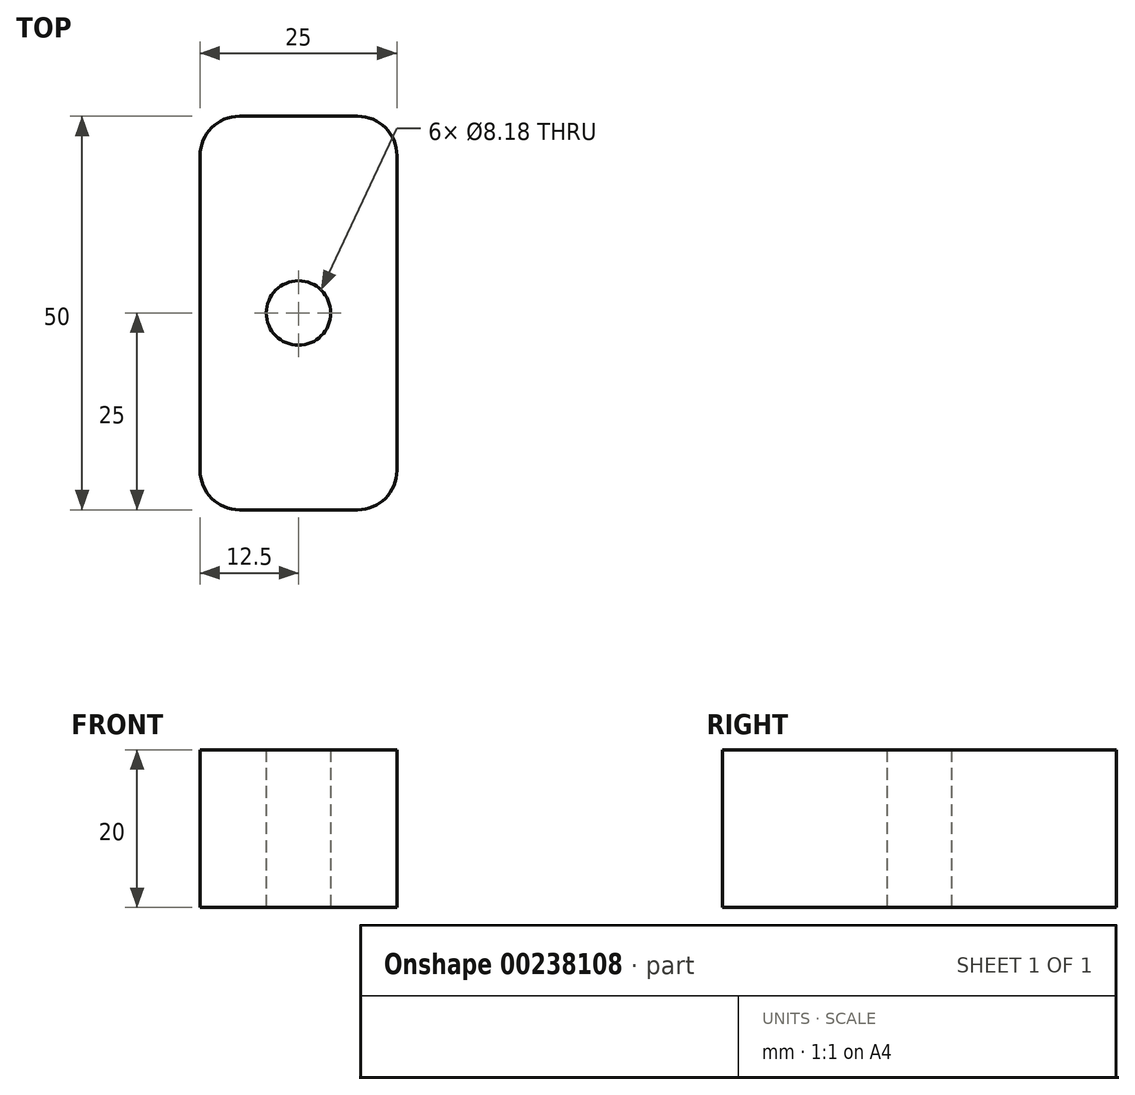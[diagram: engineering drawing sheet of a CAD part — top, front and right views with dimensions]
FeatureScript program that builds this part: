
annotation { "Feature Type Name" : "Feature", "Feature Type Description" : "" }
export const myFeature = defineFeature(function(context is Context, id is Id, definition is map)
    precondition{}
    {
        {
            var Q0;
            Q0=qCreatedBy(makeId("Top.planeOp"),FACE);
            var sketch = newSketch(context, id + "F0", { "sketchPlane" : qUnion([Q0])});
            skCircle(sketch, "E0", {"center": v(0, 0) * mm, "radius": 4.1 * mm});
            skLineSegment(sketch, "E1.bottom", {"start": v(-7.5, 25) * mm, "end": v(7.5, 25) * mm});
            skLineSegment(sketch, "E1.top", {"start": v(-7.5, -25) * mm, "end": v(7.5, -25) * mm});
            skLineSegment(sketch, "E1.left", {"start": v(-12.5, 20) * mm, "end": v(-12.5, -20) * mm});
            skLineSegment(sketch, "E1.right", {"start": v(12.5, 20) * mm, "end": v(12.5, -20) * mm});
            skLineSegment(sketch, "E2", {"start": v(0, 25) * mm, "end": v(0, -25) * mm, "construction": true});
            skPoint(sketch, "E3.visualSharp", {"position": v(-12.5, 25) * mm});
            skArc(sketch, "E3.filletArc", {"start": v(-7.5, 25) * mm, "mid": v(-11.04, 23.54) * mm, "end": v(-12.5, 20) * mm});
            skPoint(sketch, "E4.visualSharp", {"position": v(12.5, 25) * mm});
            skArc(sketch, "E4.filletArc", {"start": v(12.5, 20) * mm, "mid": v(11.04, 23.54) * mm, "end": v(7.5, 25) * mm});
            skPoint(sketch, "E5.visualSharp", {"position": v(12.5, -25) * mm});
            skArc(sketch, "E5.filletArc", {"start": v(7.5, -25) * mm, "mid": v(11.04, -23.54) * mm, "end": v(12.5, -20) * mm});
            skPoint(sketch, "E6.visualSharp", {"position": v(-12.5, -25) * mm});
            skArc(sketch, "E6.filletArc", {"start": v(-12.5, -20) * mm, "mid": v(-11.04, -23.54) * mm, "end": v(-7.5, -25) * mm});
            skSolve(sketch);
        }
        {
            var Q0;
            Q0=makeQuery(id+"F0.imprint","IMPRINT",FACE,{"disambiguationData":[TD([[makeQuery(id+"F0.imprint","IMPRINT",EDGE,{"derivedFrom":sQuery(id+"F0.wireOp",EDGE,"E0")}),-1.0]])]});
            extrude(context, id + "F1", {"entities" : qUnion([Q0]), "depth" : 20 * mm});
        }
    });
